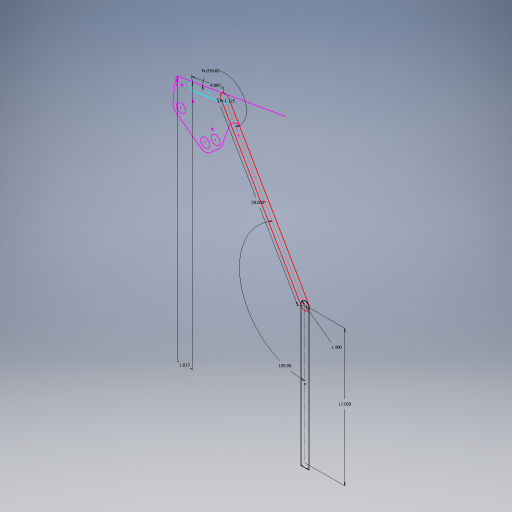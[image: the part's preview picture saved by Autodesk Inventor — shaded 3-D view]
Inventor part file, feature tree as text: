
AUTODESK INVENTOR PART (.ipt)
format: ipt  version: 2024.2 (Build 282272000, 272)  size: 292,352 bytes
history: native  units: in
note: dims shown in document units (in); Inventor stores cm internally (conversion verified against a paired STEP export)
features: other x2, sketch x1
ambient origin geometry x8: Origin, YZ Plane, XZ Plane, XY Plane, X Axis, Y Axis, Z Axis, Center Point
feature tree (3):
  other  "Blocks"
  sketch  "Sketch1"  dims[d0=17.0in d1=1.0in d2=20.0in d3=1.125in d4=4.0in d6=1.7178in d8=1.8126in]
  other  "Block1:1"
